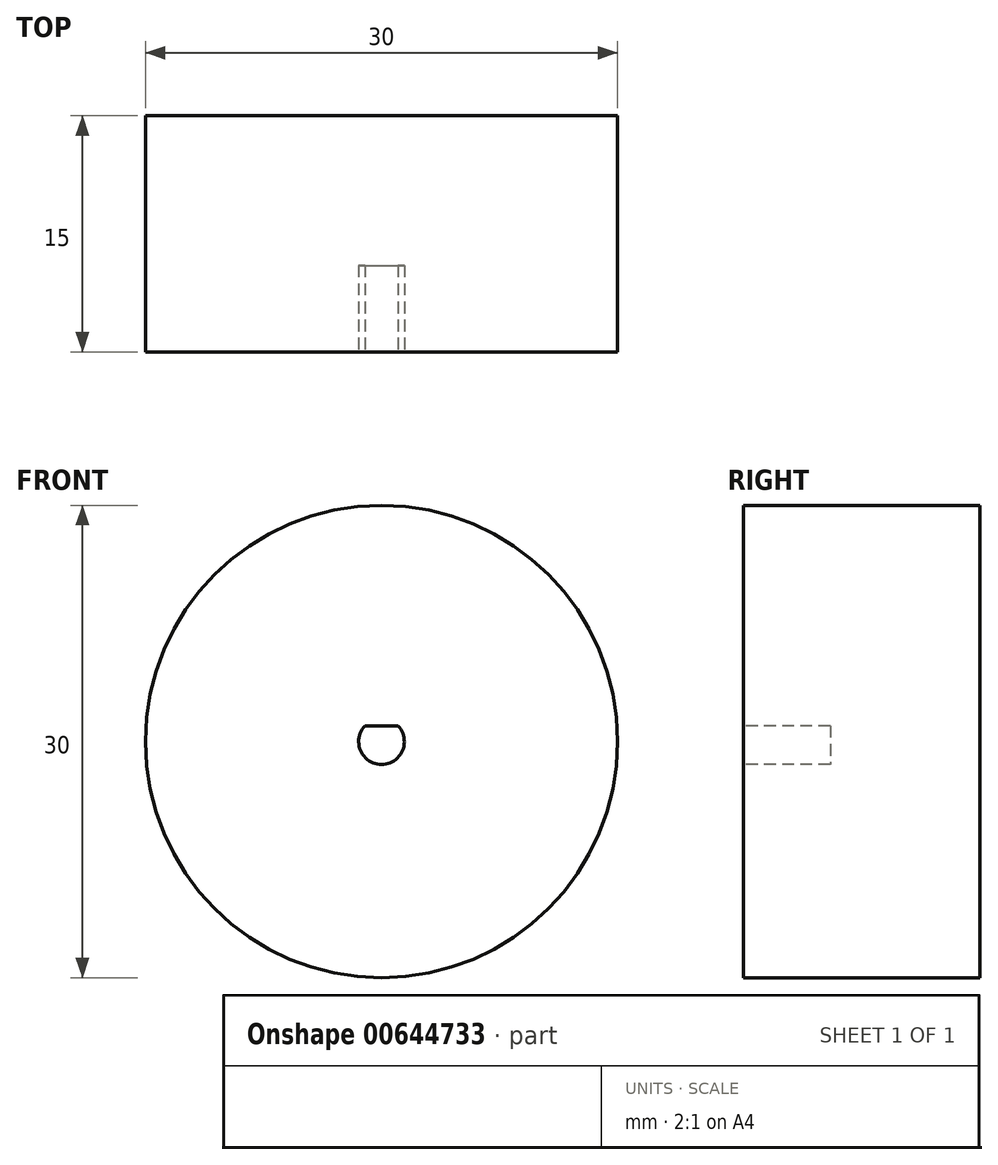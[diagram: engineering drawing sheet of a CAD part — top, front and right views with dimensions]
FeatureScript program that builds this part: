
annotation { "Feature Type Name" : "Feature", "Feature Type Description" : "" }
export const myFeature = defineFeature(function(context is Context, id is Id, definition is map)
    precondition{}
    {
        {
            var Q0;
            Q0=qCreatedBy(makeId("Front.planeOp"),FACE);
            var sketch = newSketch(context, id + "F0", { "sketchPlane" : qUnion([Q0])});
            skCircle(sketch, "E0", {"center": v(0, 0) * mm, "radius": 15 * mm});
            skSolve(sketch);
        }
        {
            var Q0;
            Q0=makeQuery(id+"F0.imprint","IMPRINT",FACE,{"disambiguationData":[TD([[makeQuery(id+"F0.imprint","IMPRINT",EDGE,{"derivedFrom":sQuery(id+"F0.wireOp",EDGE,"E0")}),1.0]])]});
            extrude(context, id + "F1", {"entities" : qUnion([Q0]), "oppositeDirection" : true, "depth" : 15 * mm, "offsetDistance" : 25 * mm});
        }
        {
            var Q0;
            Q0=makeQuery(id+"F1.opExtrude","CAP_FACE",FACE,{"disambiguationData":[OSD([sQuery(id+"F0.wireOp",EDGE,"E0")])],"isStart":true});
            var sketch = newSketch(context, id + "F2", { "sketchPlane" : qUnion([Q0])});
            skCircle(sketch, "E1", {"center": v(0, 0) * mm, "radius": 1.45 * mm});
            skLineSegment(sketch, "E2", {"start": v(-1.05, 1) * mm, "end": v(1.05, 1) * mm});
            skSolve(sketch);
        }
        {
            var Q0;
            {var subQ0=sQuery(id+"F2.wireOp",EDGE,"E2");Q0=makeQuery(id+"F2.imprint","IMPRINT",FACE,{"disambiguationData":[TD([[makeQuery(id+"F2.imprint","IMPRINT",EDGE,{"derivedFrom":subQ0}),-1.0]])]});}
            extrude(context, id + "F3", {"entities" : qUnion([Q0]), "operationType" : NewBodyOperationType.REMOVE, "oppositeDirection" : true, "depth" : 5.5 * mm, "offsetDistance" : 25 * mm});
        }
    });
